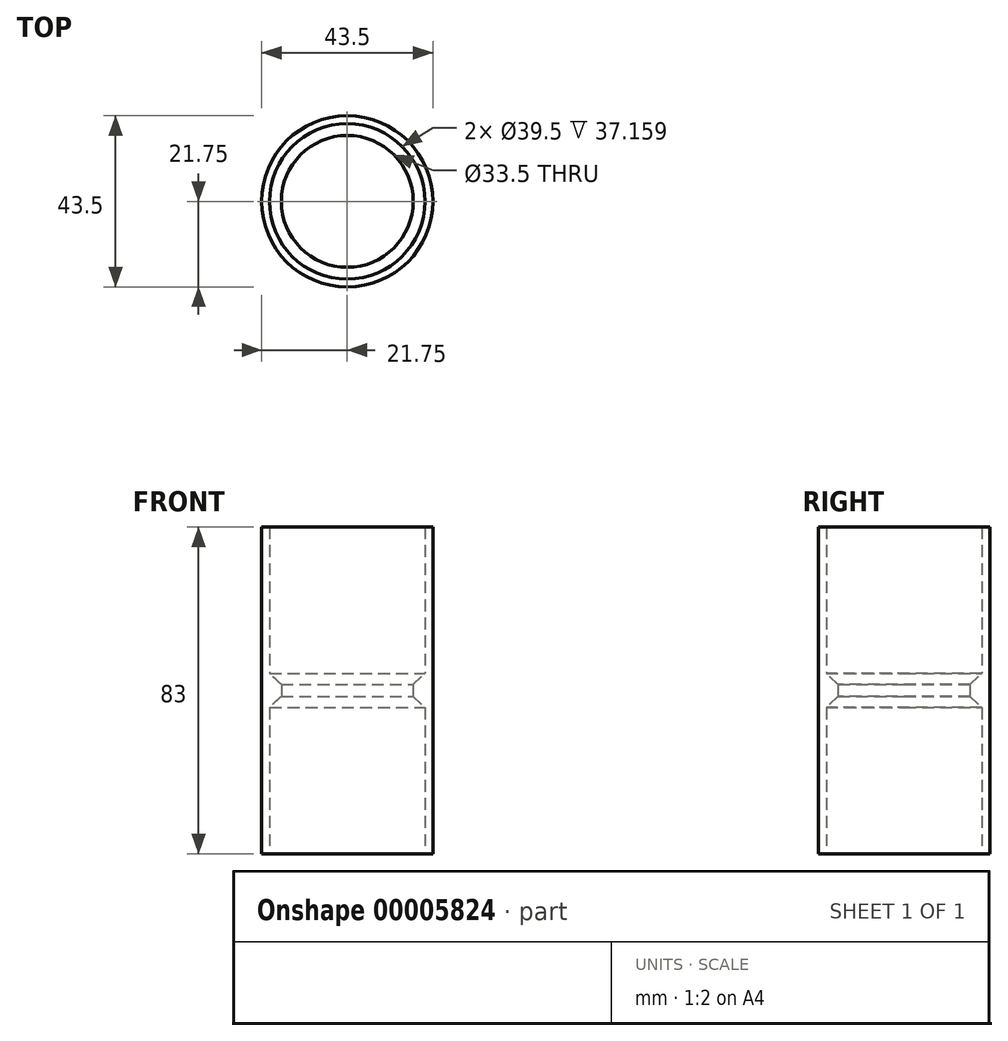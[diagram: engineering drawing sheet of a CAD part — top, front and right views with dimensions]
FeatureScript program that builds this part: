
annotation { "Feature Type Name" : "Feature", "Feature Type Description" : "" }
export const myFeature = defineFeature(function(context is Context, id is Id, definition is map)
    precondition{}
    {
        {
            var Q0;
            Q0=qCreatedBy(makeId("Front.planeOp"),FACE);
            var sketch = newSketch(context, id + "F0", { "sketchPlane" : qUnion([Q0])});
            skLineSegment(sketch, "E0.top", {"start": v(-19.75, 83) * mm, "end": v(19.75, 83) * mm});
            skLineSegment(sketch, "E0.right", {"start": v(19.75, 0) * mm, "end": v(19.75, 83) * mm});
            skLineSegment(sketch, "E1", {"start": v(-19.75, 0) * mm, "end": v(0, 0) * mm});
            skLineSegment(sketch, "E2", {"start": v(19.75, 0) * mm, "end": v(0, 0) * mm});
            skLineSegment(sketch, "E3.bottom", {"start": v(-19.75, 83) * mm, "end": v(-21.75, 83) * mm});
            skLineSegment(sketch, "E3.top", {"start": v(-19.75, 0) * mm, "end": v(-21.75, 0) * mm});
            skLineSegment(sketch, "E3.right", {"start": v(-21.75, 83) * mm, "end": v(-21.75, 0) * mm});
            skLineSegment(sketch, "E4", {"start": v(0, 0) * mm, "end": v(0, 80.5) * mm, "construction": true});
            skLineSegment(sketch, "E5.right", {"start": v(-16.75, 43) * mm, "end": v(-16.75, 40) * mm});
            skLineSegment(sketch, "E6", {"start": v(-19.75, 0) * mm, "end": v(-19.75, 37.16) * mm});
            skLineSegment(sketch, "E7", {"start": v(-19.75, 45.84) * mm, "end": v(-19.75, 83) * mm});
            skLineSegment(sketch, "E8", {"start": v(-16.75, 43) * mm, "end": v(-19.75, 45.84) * mm});
            skLineSegment(sketch, "E9", {"start": v(-16.75, 40) * mm, "end": v(-19.75, 37.16) * mm});
            skSolve(sketch);
        }
        {
            var Q0;
            Q0=makeQuery(id+"F0.imprint","IMPRINT",FACE,{"disambiguationData":[TD([[makeQuery(id+"F0.imprint","IMPRINT",EDGE,{"derivedFrom":sQuery(id+"F0.wireOp",EDGE,"E3.bottom")}),1.0]])]});
            var Q1;
            Q1=sQuery(id+"F0.wireOp",EDGE,"E4");
            revolve(context, id + "F1", {"surfaceOperationType" : NewSurfaceOperationType.NEW, "entities" : qUnion([Q0]), "axis" : qUnion([Q1]), "revolveType" : RevolveType.FULL});
        }
    });
